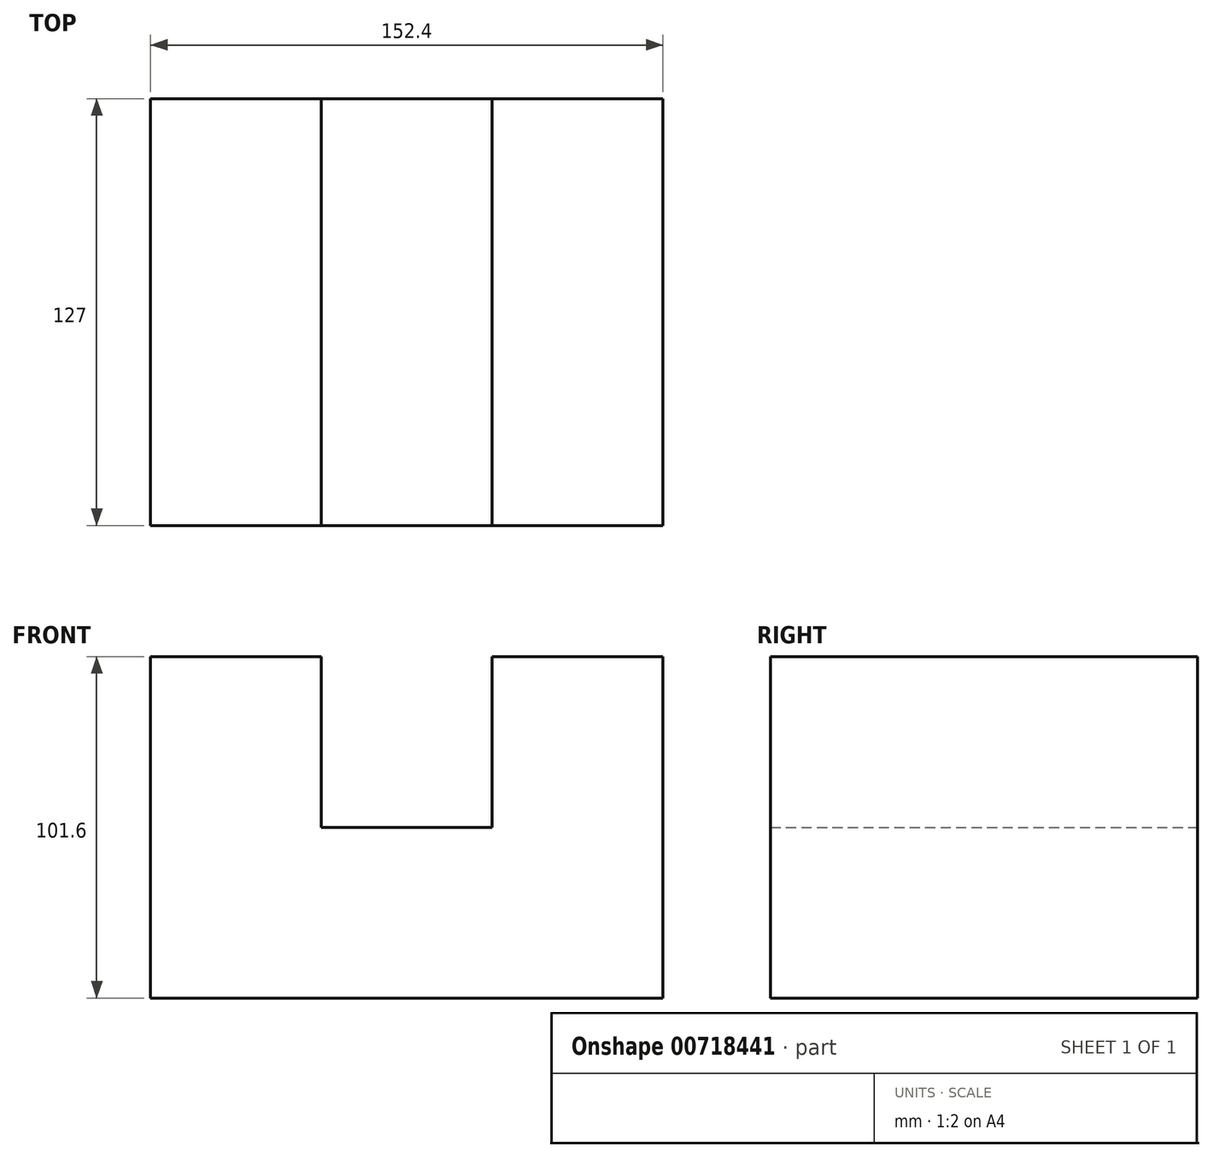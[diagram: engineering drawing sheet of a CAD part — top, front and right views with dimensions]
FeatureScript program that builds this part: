
annotation { "Feature Type Name" : "Feature", "Feature Type Description" : "" }
export const myFeature = defineFeature(function(context is Context, id is Id, definition is map)
    precondition{}
    {
        {
            var Q0;
            Q0=qCreatedBy(makeId("Front.planeOp"),FACE);
            var sketch = newSketch(context, id + "F0", { "sketchPlane" : qUnion([Q0])});
            skLineSegment(sketch, "E0", {"start": v(-43.66, -27.01) * mm, "end": v(108.74, -27.01) * mm});
            skLineSegment(sketch, "E1", {"start": v(-43.66, -27.01) * mm, "end": v(-43.66, 74.59) * mm});
            skLineSegment(sketch, "E2", {"start": v(-43.66, 74.59) * mm, "end": v(7.14, 74.59) * mm});
            skLineSegment(sketch, "E3", {"start": v(7.14, 74.59) * mm, "end": v(7.14, 23.79) * mm});
            skLineSegment(sketch, "E4", {"start": v(7.14, 23.79) * mm, "end": v(57.94, 23.79) * mm});
            skLineSegment(sketch, "E5", {"start": v(57.94, 23.79) * mm, "end": v(57.94, 74.59) * mm});
            skLineSegment(sketch, "E6", {"start": v(57.94, 74.59) * mm, "end": v(108.74, 74.59) * mm});
            skLineSegment(sketch, "E7", {"start": v(108.74, 74.59) * mm, "end": v(108.74, -27.01) * mm});
            skSolve(sketch);
        }
        {
            var Q0;
            Q0=makeQuery(id+"F0.imprint","IMPRINT",FACE,{"disambiguationData":[TD([[makeQuery(id+"F0.imprint","IMPRINT",EDGE,{"derivedFrom":sQuery(id+"F0.wireOp",EDGE,"E0")}),1.0]])]});
            extrude(context, id + "F1", {"entities" : qUnion([Q0]), "depth" : 127 * mm, "offsetDistance" : 25.4 * mm});
        }
    });
